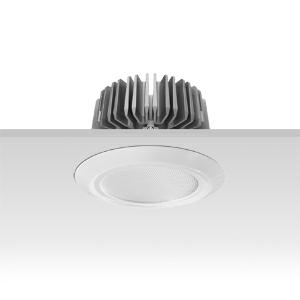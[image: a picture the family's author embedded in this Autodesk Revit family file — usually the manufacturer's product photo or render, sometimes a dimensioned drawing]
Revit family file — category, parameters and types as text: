
# Revit family: 3f_filippi_-_3f_reno_bianco_ampio_3f_filippi_-_30353_a01046_-_3f_reno_150_wh_3000-930_wide___smp_wh_7440
name_source: partatom
category: Lighting Fixtures
units: mm (PartAtom-declared; Revit-internal decimal feet)

## family parameters
Cut with Voids When Loaded = No
Host = Face
Light Source = No
Part Type = Normal
Room Calculation Point = No
Round Connector Dimension = Use Diameter
Shared = No

## types (1)
- 3F Filippi - 3F Reno Bianco Ampio (1 x LED, 2324 lm, 37 W, 3000 K)
    Apparent Load = 37 VA
    Approval mark = CE
    CIE Flux Codes = 73 92 98 100 100
    Color Rendering = 90
    Color Temperature = 3000 K
    Control Gear = Electronic ballast
    Default Elevation = 1800 mm
    Description = ILLUMINOTECHNICAL
Luminous efficiency 100% (DLOR 100%, ULOR 0%).
Initial luminous flux of the luminaire 2324 lm.
Direct symmetric wide distribution.
Installation Interdistance Transv.D = 1.01 x hu - Long.D = 1.00 x hu.
Tabular UGR (CIE 117 - 4H-8H; S=0.25H; 70/50/20): RUG 24.5 - 24.5.
Beam angle: 70° - 70°.
Luminous efficacy 63 lm/W.
Lifetime (L90/B10): 30000 h. (tq+25°C)
Lifetime (L85/B10): 50000 h. (tq+25°C)
Lifetime (L70/B10): 80000 h. (tq+25°C)
Sudden decreased luminous flux after 50000 hours: 0% (C0).
Photobiological safety in compliance with IEC/TR 62778: RG0 risk exempt, (IEC 62471).
In compliance with IEC/EN 62722-2-1 - IEC/EN 62717 standards.

SOURCE
Compact LED module 3000/930.
Energy efficiency class (UE 2019/2020 - UE 2019/2015): E.
CIE 13.3 Colour rendering index: CRI >90 (R9 >50%).
IES TM-30 Fidelity Index: Rf = 92 Rg = 101.
CCT nominal colour temperature 3000 K.
Colour initial tolerance (MacAdam): SDCM 3.
Zhaga Book 3 compliant.

MECHANICAL
Passive heat dissipator in die-casting aluminium, oversized, for optimum thermal management of the LED module.
Parabolic element with graduated/concentric rings in white polycarbonate.
Transparent external lens with glossy and satin differentiated surfaces, with a cooling and anti-insect system in methacrylate (PMMA).
Fastening spring clips in stainless steel.
Dimensions: diameter 176 mm, height 111 mm. Weight 1.395 kg.
IP44 protection degree for exposed part, IP20 for recessed part.
Mechanical strength to impacts IK05 (0.7 joule).
Glow-wire test resistance 650°C.

ELECTRICAL
Wiring on a separate unit.
Halogen Free electronic wiring 230V-50/60Hz, power factor 0.95, THD <25%, constant output current, SELV, class II, 1 driver.
Power of the luminaire 37 W.
ENEC - CE.
SAFE FLICKER: PstLM=<1 and SVM=<0.4 (IEC TR 61547-1 and IEC TR 63158), to ensure a more comfortable and safe light.
Luminaire compliant with EN 60598-2-22 for power supply from a centralised emergency system CPSS (Central Power Supply System), not incorporated in the luminaire - high risk areas excluded. The default power and flux are 100% in AC and 100% in DC.
Ambient temperature from 0°C to +25°C.
Temperature class T6 max 85°C.
Relative humidity UR: <85%.

INSTALLATION
Pull-up recessed fitting.
False ceiling carving: 150 mm.
All accessories dedicated to this product are available on the Catalog and on our website www.3F-Filippi.com.

ACCESSORIES
A01046 - Anti-glare microprismatic SMP diffuser in methacrylate (PMMA), locked and in line with the trim, in white polycarbonate.

APPLICATIONS
Suitable product for food production plants (HACCP), IFS (Food Version 6), BRC (GSFS Food Version 7).
Environments: architectural, commercial, exhibition areas, transit areas, corridors, shops, display windows, service areas.
In false ceilings with narrow voids.

WARNING
Luminaire designed for disposal/recycling at end-of-life.
Replaceable (LED only) light source by a professional. Replaceable control gear by a professional.
    Height = 0 mm  [stored 0 ft]
    Lamp = 1 x LED
    Lamp Light Flux = 2324 lm
    Lamp Power = 37 W
    Lamp count = 1
    Length = 176 mm
    Lifetime = 50000 h
    Luminous efficacy = 63 lm/W
    Manufacturer = 3F Filippi
    ModVariant = No
    Model = 3F Filippi - 30353+A01046 - 3F Reno 150 WH 3000-930 WIDE + SMP WH
    Mounting Place = Ceiling
    Mounting Type = Recessed
    Number of Poles = 1
    OnlyDefault = Yes
    Power Factor = 1
    Product Name = 3F Filippi - 3F Reno Bianco Ampio
    Product group = recessed luminaire
    ProductGroupID = 4
    Protection Class = Protection class II
    Protection Degree = IP 20
    RLX_Detail_Level = 1
    RLX_Emergency_Light_Flux = 0 lm
    RLX_Emergency_Type = 0
    RLX_Emergency_Type_DB = No
    RlxData = <blob elided: 83885 chars, md5=2c07ecdc>
    Socket = socket
    Standby Power = 0 W
    System Light Flux = 2324 lm
    System Power = 37 W
    Type Comments = Product without accessories
    Type Image = 3ffilippi_3f_reno_150_wh_vs_smp.jpg
    URL = http://relux.com
    VarID = ---
    Voltage = 0 V
    Weight = 0.00 kg
    Width = 0 mm  [stored 0 ft]

note: [stored X ft] marks values corroborated as IEEE doubles in the binary element streams (Revit-internal decimal feet)

## geometry (parser evidence)
native form markers: Blend x4, Sweep x10
no freeform markers — native parametric forms only
